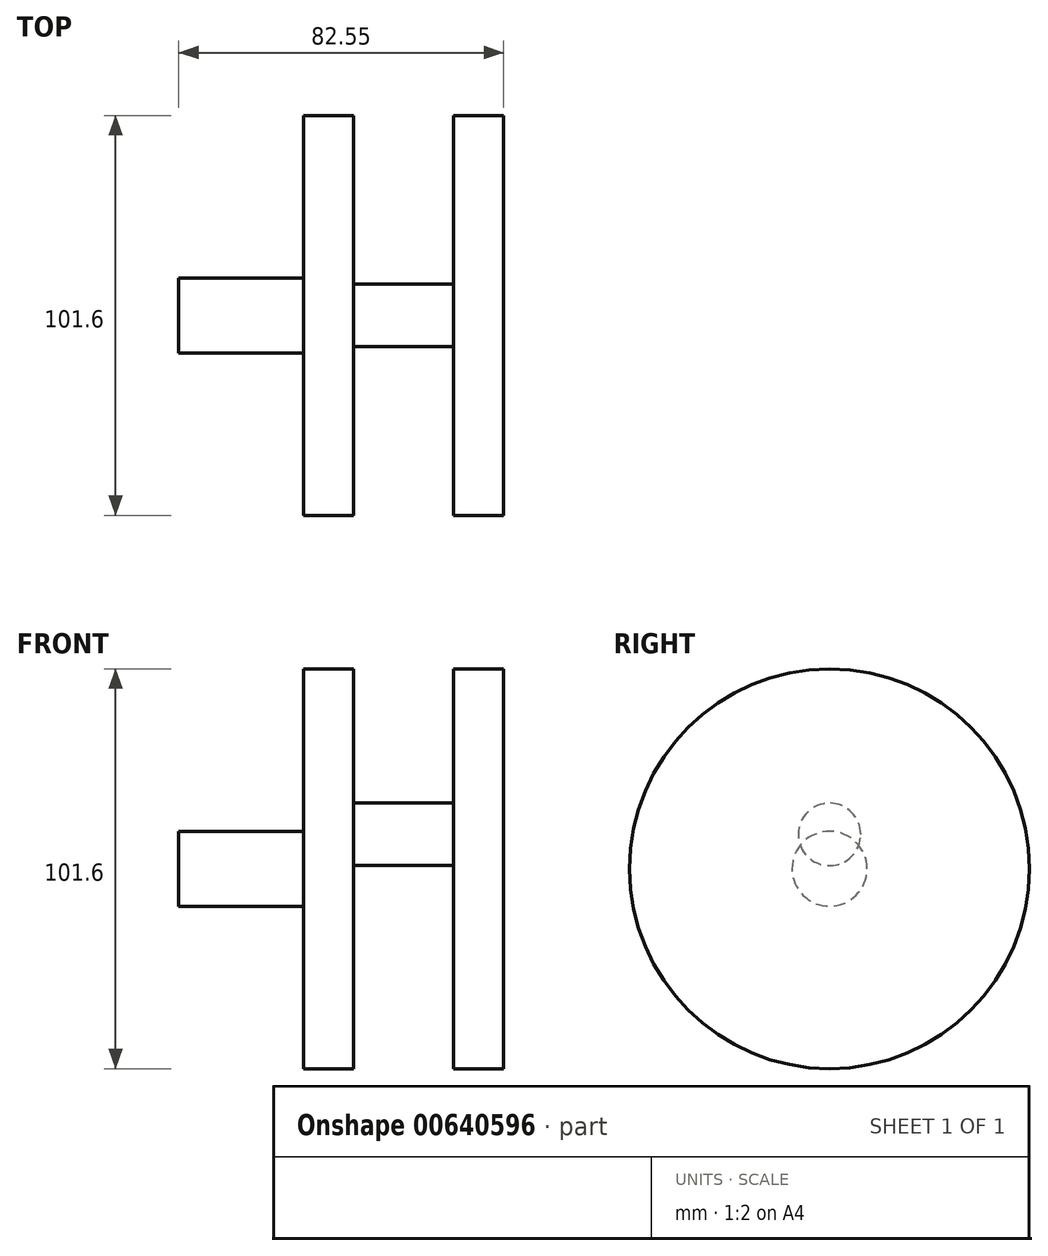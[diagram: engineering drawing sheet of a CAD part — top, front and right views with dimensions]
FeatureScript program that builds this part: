
annotation { "Feature Type Name" : "Feature", "Feature Type Description" : "" }
export const myFeature = defineFeature(function(context is Context, id is Id, definition is map)
    precondition{}
    {
        {
            var Q0;
            Q0=qCreatedBy(makeId("Front.planeOp"),FACE);
            var sketch = newSketch(context, id + "F0", { "sketchPlane" : qUnion([Q0])});
            skLineSegment(sketch, "E0.bottom", {"start": v(-25.4, 0) * mm, "end": v(-57.15, 0) * mm});
            skLineSegment(sketch, "E0.top", {"start": v(-25.4, 9.53) * mm, "end": v(-57.15, 9.53) * mm});
            skLineSegment(sketch, "E0.left", {"start": v(-25.4, 0) * mm, "end": v(-25.4, 9.53) * mm});
            skLineSegment(sketch, "E0.right", {"start": v(-57.15, 0) * mm, "end": v(-57.15, 9.53) * mm});
            skPoint(sketch, "E0.middle", {"position": v(-41.28, 4.76) * mm});
            skLineSegment(sketch, "E1.bottom", {"start": v(-25.4, 0) * mm, "end": v(-12.7, 0) * mm});
            skLineSegment(sketch, "E1.top", {"start": v(-25.4, 50.8) * mm, "end": v(-12.7, 50.8) * mm});
            skLineSegment(sketch, "E1.left", {"start": v(-25.4, 0) * mm, "end": v(-25.4, 50.8) * mm});
            skLineSegment(sketch, "E1.right", {"start": v(-12.7, 0) * mm, "end": v(-12.7, 50.8) * mm});
            skPoint(sketch, "E1.middle", {"position": v(-19.05, 25.4) * mm});
            skLineSegment(sketch, "E2.right", {"start": v(25.4, 0) * mm, "end": v(25.4, 9.52) * mm});
            skLineSegment(sketch, "E3.bottom", {"start": v(25.4, 0) * mm, "end": v(12.7, 0) * mm});
            skLineSegment(sketch, "E3.top", {"start": v(25.4, 50.8) * mm, "end": v(12.7, 50.8) * mm});
            skLineSegment(sketch, "E3.left", {"start": v(25.4, 0) * mm, "end": v(25.4, 50.8) * mm});
            skLineSegment(sketch, "E3.right", {"start": v(12.7, 0) * mm, "end": v(12.7, 50.8) * mm});
            skPoint(sketch, "E3.middle", {"position": v(19.05, 25.4) * mm});
            skLineSegment(sketch, "E4.bottom", {"start": v(-12.7, 46.83) * mm, "end": v(12.7, 46.83) * mm});
            skLineSegment(sketch, "E4.top", {"start": v(-12.7, 38.9) * mm, "end": v(12.7, 38.9) * mm});
            skLineSegment(sketch, "E4.left", {"start": v(-12.7, 46.83) * mm, "end": v(-12.7, 38.9) * mm});
            skLineSegment(sketch, "E4.right", {"start": v(12.7, 46.83) * mm, "end": v(12.7, 38.9) * mm});
            skPoint(sketch, "E4.middle", {"position": v(0, 42.86) * mm});
            skSolve(sketch);
        }
        {
            var Q0;
            {var subQ0=sQuery(id+"F0.wireOp",EDGE,"E0.bottom");Q0=makeQuery(id+"F0.imprint","IMPRINT",FACE,{"disambiguationData":[TD([[makeQuery(id+"F0.imprint","IMPRINT",EDGE,{"derivedFrom":subQ0}),-1.0]])]});}
            var Q1;
            {var subQ3=sQuery(id+"F0.wireOp",EDGE,"E1.bottom");Q1=makeQuery(id+"F0.imprint","IMPRINT",FACE,{"disambiguationData":[TD([[makeQuery(id+"F0.imprint","IMPRINT",EDGE,{"derivedFrom":subQ3}),1.0]])]});}
            var Q2;
            {var subQ3=sQuery(id+"F0.wireOp",EDGE,"E3.bottom");Q2=makeQuery(id+"F0.imprint","IMPRINT",FACE,{"disambiguationData":[TD([[makeQuery(id+"F0.imprint","IMPRINT",EDGE,{"derivedFrom":subQ3}),-1.0]])]});}
            var Q3;
            {var subQ0=sQuery(id+"F0.wireOp",EDGE,"E2.bottom");Q3=makeQuery(id+"F0.imprint","IMPRINT",FACE,{"disambiguationData":[TD([[makeQuery(id+"F0.imprint","IMPRINT",EDGE,{"derivedFrom":subQ0}),-1.0]])]});}
            var Q4;
            Q4=sQuery(id+"F0.wireOp",EDGE,"E0.bottom");
            revolve(context, id + "F1", {"entities" : qUnion([Q0, Q1, Q2, Q3]), "axis" : qUnion([Q4]), "revolveType" : RevolveType.FULL});
        }
        {
            var Q0;
            Q0=qCreatedBy(makeId("Front.planeOp"),FACE);
            var sketch = newSketch(context, id + "F2", { "sketchPlane" : qUnion([Q0])});
            skLineSegment(sketch, "E5.bottom", {"start": v(-12.7, 8.73) * mm, "end": v(12.7, 8.73) * mm});
            skLineSegment(sketch, "E5.top", {"start": v(-12.7, 16.67) * mm, "end": v(12.7, 16.67) * mm});
            skLineSegment(sketch, "E5.left", {"start": v(-12.7, 8.73) * mm, "end": v(-12.7, 16.67) * mm});
            skLineSegment(sketch, "E5.right", {"start": v(12.7, 8.73) * mm, "end": v(12.7, 16.67) * mm});
            skPoint(sketch, "E5.middle", {"position": v(0, 12.7) * mm});
            skSolve(sketch);
        }
        {
            var Q0;
            Q0=makeQuery(id+"F2.imprint","IMPRINT",FACE,{"disambiguationData":[TD([[makeQuery(id+"F2.imprint","IMPRINT",EDGE,{"derivedFrom":sQuery(id+"F2.wireOp",EDGE,"E5.bottom")}),1.0]])]});
            var Q1;
            Q1=sQuery(id+"F2.wireOp",EDGE,"E5.bottom");
            revolve(context, id + "F3", {"entities" : qUnion([Q0]), "axis" : qUnion([Q1]), "revolveType" : RevolveType.FULL});
        }
    });
